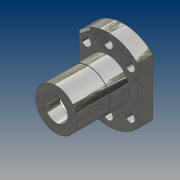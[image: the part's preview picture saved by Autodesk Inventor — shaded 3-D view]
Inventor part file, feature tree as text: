
AUTODESK INVENTOR PART (.ipt)
format: ipt  version: 2021 (Build 250183000, 183)  size: 354,304 bytes
history: native  units: in
note: dims shown in document units (in); Inventor stores cm internally (conversion verified against a paired STEP export)
features: sketch x6, extrude x5, projected_geometry x4, hole x2, pattern_circular x1, helix x1
ambient origin geometry x8: Origin, YZ Plane, XZ Plane, XY Plane, X Axis, Y Axis, Z Axis, Center Point
bodies: Solid1 (feature_tree)
feature tree (19):
  extrude  "Extrusion1"  Depth=0.315in TaperAngle=0.0deg
  extrude  "Extrusion2"  Depth=0.3937in TaperAngle=0.0deg
  extrude  "Extrusion3"  Depth=0.6693in TaperAngle=0.0deg
  extrude  "Extrusion4"  Depth=0.6693in TaperAngle=0.0deg
  hole  "Hole1"  [1 undecoded]
  pattern_circular  "Circular Pattern1"  Count=2 Angle=360.0deg
  hole  "Hole2"  [1 undecoded]
  sketch  "Sketch6"  dims[d17=1.2598in d19=0.189in d20=0.75in d21=0.375in d22=0.25in d23=0.5635in d24=1.0in d25=0.8108in d26=0.7874in d27=360.0deg d29=1.0in d30=1.0in d31=0.4724in d32=0.75in d33=0.375in d34=0.25in d35=0.5635in d36=1.0in d37=0.8108in d38=0.1181in d40=0.5315in d41=0.1575in d42=0.9843in d43=0.3937in d44=0.0in d45=90.0deg d46=90.0deg d47=0.0in d48=0.0in d49=0.2362in d50=0.0197in d51=0.0in]
  helix  "Coil1"  [1 undecoded]
  extrude  "Extrusion5"  Depth=0.0197in
  sketch  "Sketch1"  dims[d0=1.6535in d2=0.315in d3=0.0in]
  sketch  "Sketch2"  dims[d4=0.8661in d6=0.3937in d7=0.0in]
  projected_geometry  "Projected Loop1"
  sketch  "Sketch3"  dims[d8=0.8465in d10=0.6693in d11=0.0in]
  sketch  "Sketch4"  dims[d12=1.1811in d13=0.6693in d14=0.0in]
  projected_geometry  "Projected Loop2"
  sketch  "Sketch5"  dims[d15=45.0deg d16=45.0deg]
  projected_geometry  "Projected Loop3"
  projected_geometry  "Project Cut Edges1"
note: 3 required parameter values undecoded (feature->parameter linkage not recoverable at this tier; creation-order binding heuristic only, values carry confidence <= 0.55)
